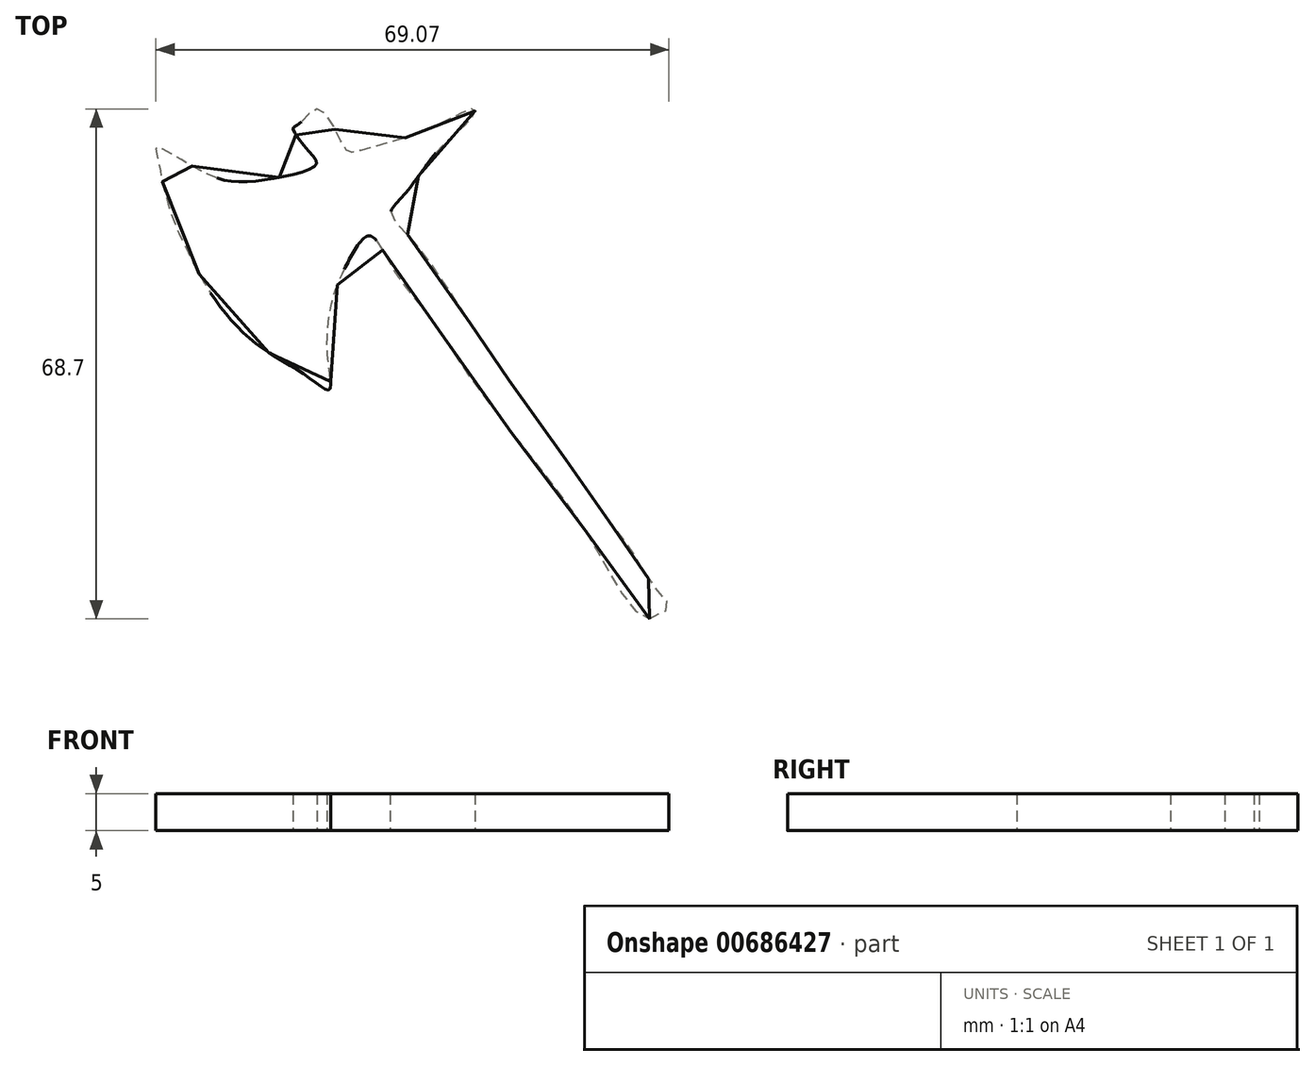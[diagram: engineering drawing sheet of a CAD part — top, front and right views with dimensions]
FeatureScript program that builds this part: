
annotation { "Feature Type Name" : "Feature", "Feature Type Description" : "" }
export const myFeature = defineFeature(function(context is Context, id is Id, definition is map)
    precondition{}
    {
        {
            var Q0;
            Q0=qCreatedBy(makeId("Top.planeOp"),FACE);
            var sketch = newSketch(context, id + "F0", { "sketchPlane" : qUnion([Q0])});
            skFitSpline(sketch, "E0", {"points": [v(-2.54, 0) * mm, v(0, 1.57) * mm, v(0, 2.12) * mm, v(-1.58, 4.06) * mm, v(-3.65, 6.96) * mm, v(-5.09, 9.48) * mm, v(-7.88, 13.03) * mm, v(-9.8, 15.82) * mm, v(-12, 18.95) * mm, v(-15.95, 24.59) * mm, v(-19.6, 29.58) * mm, v(-24.37, 36.38) * mm, v(-25.17, 37.56) * mm, v(-26.21, 39.14) * mm, v(-29.8, 44.74) * mm, v(-35.66, 52.36) * mm, v(-37.42, 54.51) * mm, v(-35.27, 57.44) * mm, v(-30.77, 63.3) * mm, v(-26.67, 67.21) * mm, v(-26.08, 68.66) * mm, v(-30.77, 66.63) * mm, v(-35.27, 64.87) * mm, v(-42.1, 62.91) * mm, v(-43.47, 63.3) * mm, v(-46.99, 68.66) * mm, v(-49.73, 66.63) * mm, v(-50.5, 66.04) * mm, v(-48.16, 62.72) * mm, v(-47.38, 61.16) * mm, v(-52.66, 59.4) * mm, v(-59.3, 59) * mm, v(-64.38, 61.16) * mm, v(-68.87, 63.5) * mm, v(-68.87, 62.72) * mm, v(-67.5, 56.47) * mm, v(-64.97, 50.02) * mm, v(-60.86, 42.79) * mm, v(-55, 36.73) * mm, v(-48.55, 32.63) * mm, v(-45.62, 30.87) * mm, v(-45.82, 35.17) * mm, v(-45.23, 42.79) * mm, v(-42.89, 48.46) * mm, v(-40.15, 51.58) * mm, v(-37.03, 47.09) * mm, v(-32.53, 41.23) * mm, v(-27.26, 33.41) * mm, v(-20.22, 24.03) * mm, v(-13.19, 14.85) * mm, v(-8.9, 8.01) * mm, v(-2.54, 0) * mm]});
            skSolve(sketch);
        }
        {
            var Q0;
            Q0 = qSketchRegion(id + "F0", true);
            extrude(context, id + "F1", {"entities" : qUnion([Q0]), "depth" : 5 * mm, "offsetDistance" : 25.4 * mm});
        }
    });
